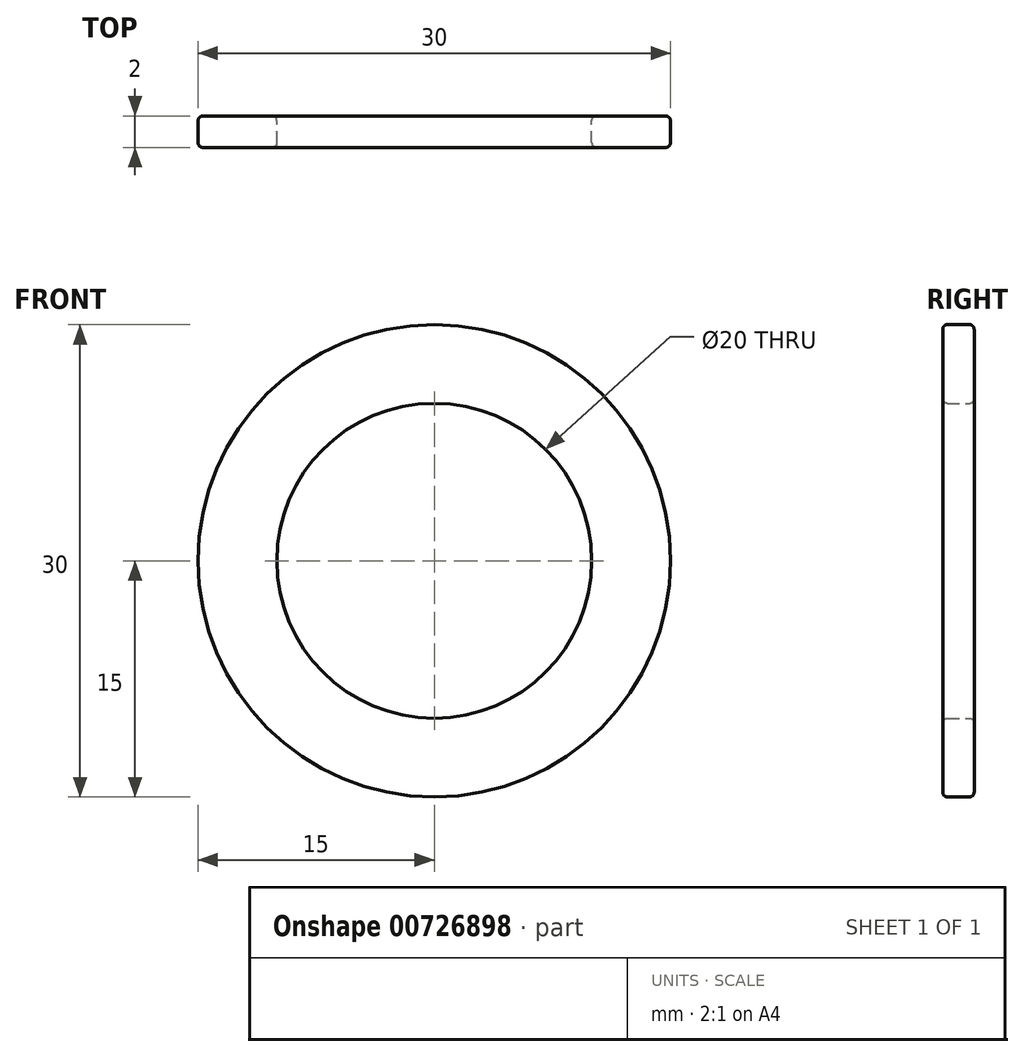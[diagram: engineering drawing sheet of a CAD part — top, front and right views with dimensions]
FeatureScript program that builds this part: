
annotation { "Feature Type Name" : "Feature", "Feature Type Description" : "" }
export const myFeature = defineFeature(function(context is Context, id is Id, definition is map)
    precondition{}
    {
        {
            var Q0;
            Q0=qCreatedBy(makeId("Front.planeOp"),FACE);
            var sketch = newSketch(context, id + "F0", { "sketchPlane" : qUnion([Q0])});
            skCircle(sketch, "E0", {"center": v(0, 0) * mm, "radius": 10 * mm});
            skCircle(sketch, "E1", {"center": v(0, 0) * mm, "radius": 15 * mm});
            skSolve(sketch);
        }
        {
            var Q0;
            Q0 = qSketchRegion(id + "F0", true);
            extrude(context, id + "F1", {"entities" : qUnion([Q0]), "depth" : 2 * mm, "offsetDistance" : 25 * mm});
        }
        {
            var Q0;
            Q0=makeQuery(id+"F1.opExtrude","CAP_EDGE",EDGE,{"disambiguationData":[OSD([sQuery(id+"F0.wireOp",EDGE,"E0")])],"isStart":true});
            var Q1;
            Q1=makeQuery(id+"F1.opExtrude","CAP_EDGE",EDGE,{"disambiguationData":[OSD([sQuery(id+"F0.wireOp",EDGE,"E0")])],"isStart":false});
            var Q2;
            Q2=makeQuery(id+"F1.opExtrude","CAP_EDGE",EDGE,{"disambiguationData":[OSD([sQuery(id+"F0.wireOp",EDGE,"E1")])],"isStart":false});
            var Q3;
            Q3=makeQuery(id+"F1.opExtrude","CAP_EDGE",EDGE,{"disambiguationData":[OSD([sQuery(id+"F0.wireOp",EDGE,"E1")])],"isStart":true});
            fillet(context, id + "F2", {"entities" : qUnion([Q0, Q1, Q2, Q3]), "radius" : 0.3 * mm, "tangentPropagation" : true, "allowEdgeOverflow" : false});
        }
    });
